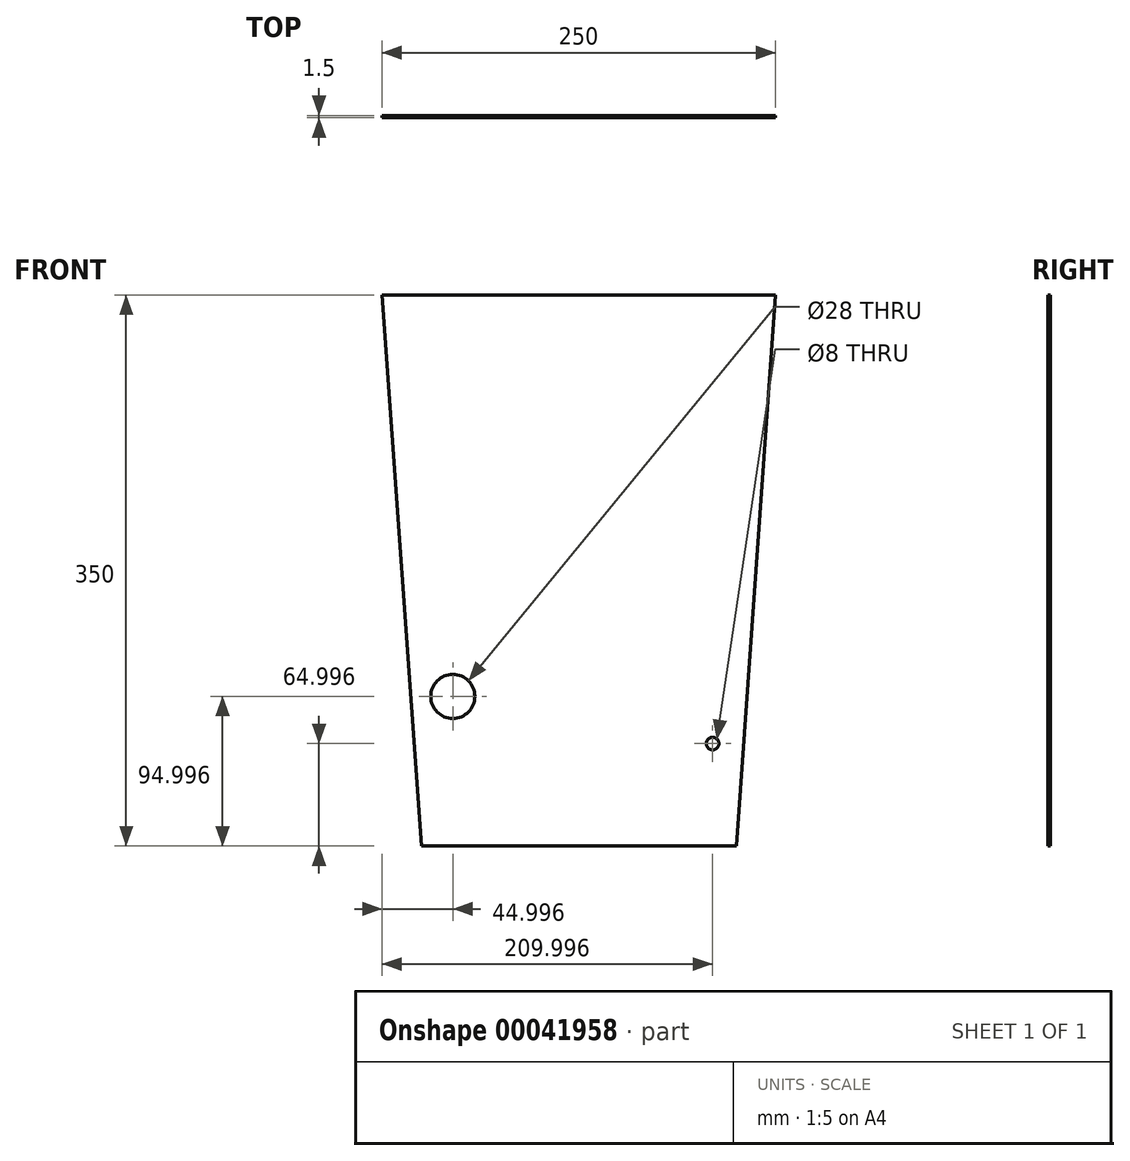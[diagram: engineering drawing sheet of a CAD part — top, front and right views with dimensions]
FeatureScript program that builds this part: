
annotation { "Feature Type Name" : "Feature", "Feature Type Description" : "" }
export const myFeature = defineFeature(function(context is Context, id is Id, definition is map)
    precondition{}
    {
        {
            var Q0;
            Q0=qCreatedBy(makeId("Front.planeOp"),FACE);
            var sketch = newSketch(context, id + "F0", { "sketchPlane" : qUnion([Q0])});
            skLineSegment(sketch, "E0", {"start": v(0.05, 74.16) * mm, "end": v(0.05, -275.84) * mm});
            skLineSegment(sketch, "E1", {"start": v(-124.95, 74.16) * mm, "end": v(125.05, 74.16) * mm});
            skLineSegment(sketch, "E2", {"start": v(-99.95, -275.84) * mm, "end": v(100.05, -275.84) * mm});
            skLineSegment(sketch, "E3", {"start": v(-124.95, 74.16) * mm, "end": v(-99.95, -275.84) * mm});
            skLineSegment(sketch, "E4", {"start": v(125.05, 74.16) * mm, "end": v(100.05, -275.84) * mm});
            skSolve(sketch);
        }
        {
            var Q0;
            {var subQ2=sQuery(id+"F0.wireOp",EDGE,"E0");Q0=makeQuery(id+"F0.imprint","IMPRINT",FACE,{"disambiguationData":[TD([[makeQuery(id+"F0.imprint","IMPRINT",EDGE,{"derivedFrom":subQ2}),1.0]])]});}
            var Q1;
            {var subQ2=sQuery(id+"F0.wireOp",EDGE,"E0");Q1=makeQuery(id+"F0.imprint","IMPRINT",FACE,{"disambiguationData":[TD([[makeQuery(id+"F0.imprint","IMPRINT",EDGE,{"derivedFrom":subQ2}),-1.0]])]});}
            extrude(context, id + "F1", {"entities" : qUnion([Q0, Q1]), "depth" : 1.5 * mm});
        }
        {
            var Q0;
            Q0=makeQuery(id+"F1.opExtrude","CAP_FACE",FACE,{"disambiguationData":[OSD([sQuery(id+"F0.wireOp",EDGE,"E1"),sQuery(id+"F0.wireOp",EDGE,"E2"),sQuery(id+"F0.wireOp",EDGE,"E3"),sQuery(id+"F0.wireOp",EDGE,"E4")])],"isStart":false});
            var sketch = newSketch(context, id + "F2", { "sketchPlane" : qUnion([Q0])});
            skLineSegment(sketch, "E5", {"start": v(-137.15, -180.84) * mm, "end": v(-27.84, -180.84) * mm});
            skLineSegment(sketch, "E6", {"start": v(-79.95, -110.97) * mm, "end": v(-79.95, -229.72) * mm});
            skLineSegment(sketch, "E7", {"start": v(85.05, -174.12) * mm, "end": v(85.05, -269.48) * mm});
            skLineSegment(sketch, "E8", {"start": v(36.03, -210.84) * mm, "end": v(99.9, -210.84) * mm});
            skPoint(sketch, "E9", {"position": v(-79.95, -180.84) * mm});
            skPoint(sketch, "E10", {"position": v(85.05, -210.84) * mm});
            skSolve(sketch);
        }
        {
            var Q0;
            Q0=sQuery(id+"F2.wireOp",VERTEX,"E9");
            var Q1;
            Q1=makeQuery(id+"F1.opExtrude","SWEPT_BODY",BODY,{"disambiguationData":[OSD([sQuery(id+"F0.wireOp",EDGE,"E1"),sQuery(id+"F0.wireOp",EDGE,"E2"),sQuery(id+"F0.wireOp",EDGE,"E3"),sQuery(id+"F0.wireOp",EDGE,"E4")])]});
            hole(context, id + "F3", {"style" : HoleStyle.SIMPLE, "holeDiameter" : 28 * mm, "endStyle" : HoleEndStyle.THROUGH, "locations" : qUnion([Q0]), "scope" : qUnion([Q1])});
        }
        {
            var Q0;
            Q0=sQuery(id+"F2.wireOp",VERTEX,"E10");
            var Q1;
            Q1=makeQuery(id+"F1.opExtrude","SWEPT_BODY",BODY,{"disambiguationData":[OSD([sQuery(id+"F0.wireOp",EDGE,"E1"),sQuery(id+"F0.wireOp",EDGE,"E2"),sQuery(id+"F0.wireOp",EDGE,"E3"),sQuery(id+"F0.wireOp",EDGE,"E4")])]});
            hole(context, id + "F4", {"style" : HoleStyle.SIMPLE, "holeDiameter" : 8 * mm, "endStyle" : HoleEndStyle.THROUGH, "locations" : qUnion([Q0]), "scope" : qUnion([Q1])});
        }
    });
